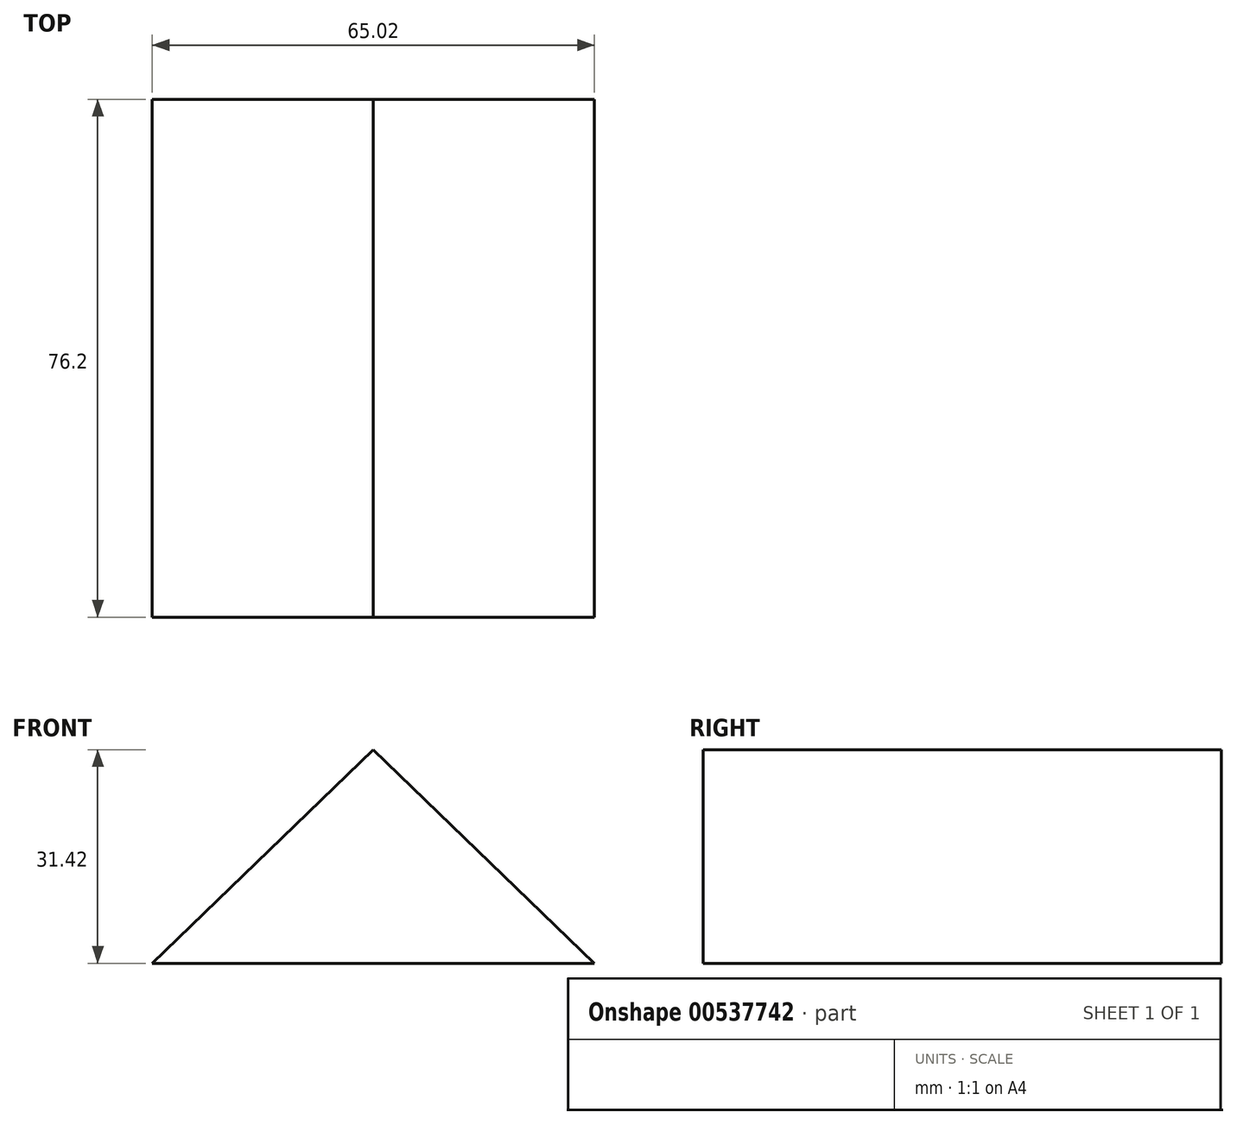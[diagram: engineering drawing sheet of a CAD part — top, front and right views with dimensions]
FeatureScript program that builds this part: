
annotation { "Feature Type Name" : "Feature", "Feature Type Description" : "" }
export const myFeature = defineFeature(function(context is Context, id is Id, definition is map)
    precondition{}
    {
        {
            var Q0;
            Q0=qCreatedBy(makeId("Front.planeOp"),FACE);
            var sketch = newSketch(context, id + "F0", { "sketchPlane" : qUnion([Q0])});
            skLineSegment(sketch, "E0", {"start": v(-40.3, 27.55) * mm, "end": v(-72.8, -3.87) * mm});
            skLineSegment(sketch, "E1", {"start": v(-40.3, 27.55) * mm, "end": v(-7.78, -3.87) * mm});
            skLineSegment(sketch, "E2", {"start": v(-7.78, -3.87) * mm, "end": v(-72.8, -3.87) * mm});
            skLineSegment(sketch, "E3", {"start": v(-40.3, 27.55) * mm, "end": v(-40.3, -3.87) * mm});
            skSolve(sketch);
        }
        {
            var Q0;
            Q0 = qSketchRegion(id + "F0", true);
            extrude(context, id + "F1", {"entities" : qUnion([Q0]), "depth" : 76.2 * mm, "offsetDistance" : 25.4 * mm});
        }
    });
